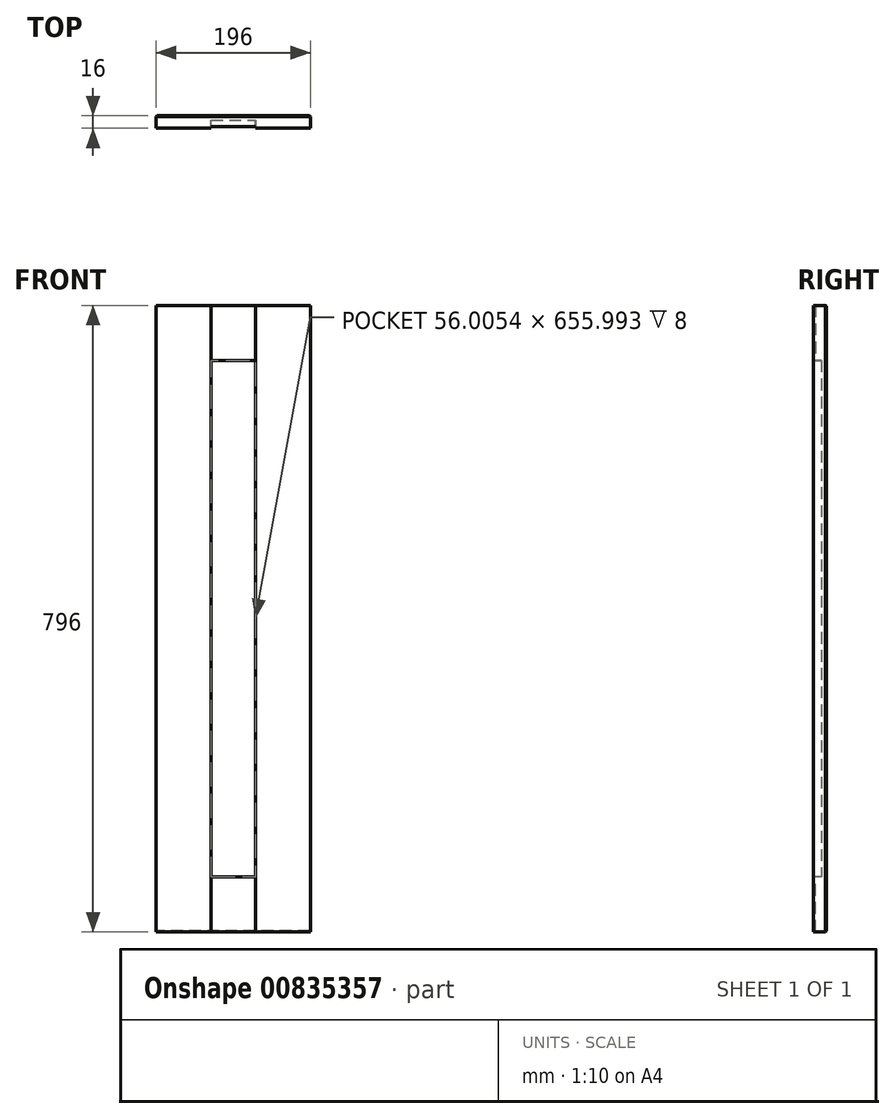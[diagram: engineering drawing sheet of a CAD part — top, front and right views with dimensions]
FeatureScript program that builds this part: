
annotation { "Feature Type Name" : "Feature", "Feature Type Description" : "" }
export const myFeature = defineFeature(function(context is Context, id is Id, definition is map)
    precondition{}
    {
        {
            var Q0;
            Q0=qCreatedBy(makeId("Front.planeOp"),FACE);
            var sketch = newSketch(context, id + "F0", { "sketchPlane" : qUnion([Q0])});
            skLineSegment(sketch, "E0.bottom", {"start": v(0, 0) * mm, "end": v(35.9, 0) * mm});
            skLineSegment(sketch, "E0.top", {"start": v(0, 30.12) * mm, "end": v(35.9, 30.12) * mm});
            skLineSegment(sketch, "E0.left", {"start": v(0, 0) * mm, "end": v(0, 30.12) * mm});
            skLineSegment(sketch, "E0.right", {"start": v(35.9, 0) * mm, "end": v(35.9, 30.12) * mm});
            skSolve(sketch);
        }
        {
            var Q0;
            Q0=makeQuery(id+"F0.imprint","IMPRINT",FACE,{"disambiguationData":[TD([[makeQuery(id+"F0.imprint","IMPRINT",EDGE,{"derivedFrom":sQuery(id+"F0.wireOp",EDGE,"E0.bottom")}),1.0]])]});
            extrude(context, id + "F1", {"entities" : qUnion([Q0]), "depth" : 16 * mm, "offsetDistance" : 25.4 * mm});
        }
        {
            var Q0;
            Q0=makeQuery(id+"F1.opExtrude","SWEPT_FACE",FACE,{"disambiguationData":[OSD([sQuery(id+"F0.wireOp",EDGE,"E0.left")])]});
            extrude(context, id + "F2", {"entities" : qUnion([Q0]), "operationType" : NewBodyOperationType.ADD, "oppositeDirection" : true, "depth" : 196 * mm, "offsetDistance" : 25 * mm});
        }
        {
            var Q0;
            {var subQ0=sQuery(id+"F0.wireOp",EDGE,"E0.bottom");Q0=makeQuery(id+"F2.boolean.opBoolean","MERGE",FACE,{"derivedFrom":[makeQuery(id+"F1.opExtrude","SWEPT_FACE",FACE,{"disambiguationData":[OSD([subQ0])]}),makeQuery(id+"F2.opExtrude","SWEPT_FACE",FACE,{"disambiguationData":[OSD([subQ0,sQuery(id+"F0.wireOp",EDGE,"E0.left")])]})]});}
            extrude(context, id + "F3", {"entities" : qUnion([Q0]), "operationType" : NewBodyOperationType.ADD, "oppositeDirection" : true, "depth" : 796 * mm, "offsetDistance" : 25 * mm});
        }
        {
            var Q0;
            {var subQ0=sQuery(id+"F0.wireOp",EDGE,"E0.left");var subQ1=sQuery(id+"F0.wireOp",EDGE,"E0.bottom");Q0=makeQuery(id+"F3.boolean.opBoolean","MERGE",FACE,{"derivedFrom":[makeQuery(id+"F2.boolean.opBoolean","MERGE",FACE,{"derivedFrom":[makeQuery(id+"F1.opExtrude","CAP_FACE",FACE,{"disambiguationData":[OSD([subQ1,sQuery(id+"F0.wireOp",EDGE,"E0.top"),subQ0,sQuery(id+"F0.wireOp",EDGE,"E0.right")])],"isStart":false}),makeQuery(id+"F2.opExtrude","SWEPT_FACE",FACE,{"disambiguationData":[OSD([subQ0]),TDD([makeQuery(id+"F1.opExtrude","CAP_EDGE",EDGE,{"disambiguationData":[OSD([subQ0])],"isStart":false})])]})]}),makeQuery(id+"F3.opExtrude","SWEPT_FACE",FACE,{"disambiguationData":[OSD([subQ1,subQ0]),TDD([makeQuery(id+"F2.boolean.opBoolean","MERGE",EDGE,{"derivedFrom":[makeQuery(id+"F1.opExtrude","CAP_EDGE",EDGE,{"disambiguationData":[OSD([subQ1])],"isStart":false}),makeQuery(id+"F2.opExtrude","SWEPT_EDGE",EDGE,{"disambiguationData":[OSD([subQ1,subQ0]),TDD([makeQuery(id+"F1.opExtrude","CAP_VERTEX",VERTEX,{"disambiguationData":[OSD([subQ1,subQ0])],"isStart":false})])]})]})])]})]});}
            var sketch = newSketch(context, id + "F4", { "sketchPlane" : qUnion([Q0])});
            skLineSegment(sketch, "E1.bottom", {"start": v(0, 796) * mm, "end": v(42.19, 796) * mm});
            skLineSegment(sketch, "E1.top", {"start": v(0, 751.57) * mm, "end": v(42.19, 751.57) * mm});
            skLineSegment(sketch, "E1.left", {"start": v(0, 796) * mm, "end": v(0, 751.57) * mm});
            skLineSegment(sketch, "E1.right", {"start": v(42.19, 796) * mm, "end": v(42.19, 751.57) * mm});
            skLineSegment(sketch, "E2.bottom", {"start": v(196, 796) * mm, "end": v(153.6, 796) * mm});
            skLineSegment(sketch, "E2.top", {"start": v(196, 746.75) * mm, "end": v(153.6, 746.75) * mm});
            skLineSegment(sketch, "E2.left", {"start": v(196, 796) * mm, "end": v(196, 746.75) * mm});
            skLineSegment(sketch, "E2.right", {"start": v(153.6, 796) * mm, "end": v(153.6, 746.75) * mm});
            skSolve(sketch);
        }
        {
            var Q0;
            Q0=makeQuery(id+"F4.imprint","IMPRINT",FACE,{"disambiguationData":[TD([[makeQuery(id+"F4.imprint","IMPRINT",EDGE,{"derivedFrom":sQuery(id+"F4.wireOp",EDGE,"E1.bottom")}),-1.0]])]});
            var Q1;
            Q1=makeQuery(id+"F4.imprint","IMPRINT",FACE,{"disambiguationData":[TD([[makeQuery(id+"F4.imprint","IMPRINT",EDGE,{"derivedFrom":sQuery(id+"F4.wireOp",EDGE,"E2.bottom")}),-1.0]])]});
            extrude(context, id + "F5", {"entities" : qUnion([Q0, Q1]), "operationType" : NewBodyOperationType.ADD, "depth" : 25 * mm, "offsetDistance" : 25 * mm});
        }
        {
            var Q0;
            {var subQ0=sQuery(id+"F0.wireOp",EDGE,"E0.left");var subQ1=sQuery(id+"F0.wireOp",EDGE,"E0.bottom");Q0=makeQuery(id+"F3.boolean.opBoolean","MERGE",FACE,{"derivedFrom":[makeQuery(id+"F2.boolean.opBoolean","MERGE",FACE,{"derivedFrom":[makeQuery(id+"F1.opExtrude","CAP_FACE",FACE,{"disambiguationData":[OSD([subQ1,sQuery(id+"F0.wireOp",EDGE,"E0.top"),subQ0,sQuery(id+"F0.wireOp",EDGE,"E0.right")])],"isStart":false}),makeQuery(id+"F2.opExtrude","SWEPT_FACE",FACE,{"disambiguationData":[OSD([subQ0]),TDD([makeQuery(id+"F1.opExtrude","CAP_EDGE",EDGE,{"disambiguationData":[OSD([subQ0])],"isStart":false})])]})]}),makeQuery(id+"F3.opExtrude","SWEPT_FACE",FACE,{"disambiguationData":[OSD([subQ1,subQ0]),TDD([makeQuery(id+"F2.boolean.opBoolean","MERGE",EDGE,{"derivedFrom":[makeQuery(id+"F1.opExtrude","CAP_EDGE",EDGE,{"disambiguationData":[OSD([subQ1])],"isStart":false}),makeQuery(id+"F2.opExtrude","SWEPT_EDGE",EDGE,{"disambiguationData":[OSD([subQ1,subQ0]),TDD([makeQuery(id+"F1.opExtrude","CAP_VERTEX",VERTEX,{"disambiguationData":[OSD([subQ1,subQ0])],"isStart":false})])]})]})])]})]});}
            var sketch = newSketch(context, id + "F6", { "sketchPlane" : qUnion([Q0])});
            skLineSegment(sketch, "E3.bottom", {"start": v(196, 0) * mm, "end": v(163.38, 0) * mm});
            skLineSegment(sketch, "E3.top", {"start": v(196, 46.55) * mm, "end": v(163.38, 46.55) * mm});
            skLineSegment(sketch, "E3.left", {"start": v(196, 0) * mm, "end": v(196, 46.55) * mm});
            skLineSegment(sketch, "E3.right", {"start": v(163.38, 0) * mm, "end": v(163.38, 46.55) * mm});
            skLineSegment(sketch, "E4.bottom", {"start": v(0, 0) * mm, "end": v(50.28, 0) * mm});
            skLineSegment(sketch, "E4.top", {"start": v(0, 44.4) * mm, "end": v(50.28, 44.4) * mm});
            skLineSegment(sketch, "E4.left", {"start": v(0, 0) * mm, "end": v(0, 44.4) * mm});
            skLineSegment(sketch, "E4.right", {"start": v(50.28, 0) * mm, "end": v(50.28, 44.4) * mm});
            skSolve(sketch);
        }
        {
            var Q0;
            Q0=makeQuery(id+"F6.imprint","IMPRINT",FACE,{"disambiguationData":[TD([[makeQuery(id+"F6.imprint","IMPRINT",EDGE,{"derivedFrom":sQuery(id+"F6.wireOp",EDGE,"E3.bottom")}),1.0]])]});
            var Q1;
            Q1=makeQuery(id+"F6.imprint","IMPRINT",FACE,{"disambiguationData":[TD([[makeQuery(id+"F6.imprint","IMPRINT",EDGE,{"derivedFrom":sQuery(id+"F6.wireOp",EDGE,"E4.bottom")}),1.0]])]});
            extrude(context, id + "F7", {"entities" : qUnion([Q0, Q1]), "operationType" : NewBodyOperationType.ADD, "depth" : 25 * mm, "offsetDistance" : 25 * mm});
        }
        {
            var Q0;
            Q0=makeQuery(id+"F7.opExtrude","SWEPT_FACE",FACE,{"disambiguationData":[OSD([sQuery(id+"F6.wireOp",EDGE,"E4.right")])]});
            extrude(context, id + "F8", {"entities" : qUnion([Q0]), "operationType" : NewBodyOperationType.ADD, "depth" : 19.72 * mm, "offsetDistance" : 25 * mm});
        }
        {
            var Q0;
            {var subQ0=sQuery(id+"F6.wireOp",EDGE,"E4.top");Q0=makeQuery(id+"F8.boolean.opBoolean","MERGE",FACE,{"derivedFrom":[makeQuery(id+"F7.opExtrude","SWEPT_FACE",FACE,{"disambiguationData":[OSD([subQ0])]}),makeQuery(id+"F8.opExtrude","SWEPT_FACE",FACE,{"disambiguationData":[OSD([subQ0,sQuery(id+"F6.wireOp",EDGE,"E4.right")])]})]});}
            extrude(context, id + "F9", {"entities" : qUnion([Q0]), "operationType" : NewBodyOperationType.ADD, "depth" : 25.6 * mm, "offsetDistance" : 25 * mm});
        }
        {
            var Q0;
            Q0=makeQuery(id+"F7.opExtrude","SWEPT_FACE",FACE,{"disambiguationData":[OSD([sQuery(id+"F6.wireOp",EDGE,"E3.right")])]});
            extrude(context, id + "F10", {"entities" : qUnion([Q0]), "operationType" : NewBodyOperationType.ADD, "depth" : 37.38 * mm, "offsetDistance" : 25 * mm});
        }
        {
            var Q0;
            {var subQ0=sQuery(id+"F6.wireOp",EDGE,"E3.top");Q0=makeQuery(id+"F10.boolean.opBoolean","MERGE",FACE,{"derivedFrom":[makeQuery(id+"F7.opExtrude","SWEPT_FACE",FACE,{"disambiguationData":[OSD([subQ0])]}),makeQuery(id+"F10.opExtrude","SWEPT_FACE",FACE,{"disambiguationData":[OSD([subQ0,sQuery(id+"F6.wireOp",EDGE,"E3.right")])]})]});}
            extrude(context, id + "F11", {"entities" : qUnion([Q0]), "operationType" : NewBodyOperationType.ADD, "depth" : 23.45 * mm, "offsetDistance" : 25 * mm});
        }
        {
            var Q0;
            Q0=makeQuery(id+"F5.opExtrude","SWEPT_FACE",FACE,{"disambiguationData":[OSD([sQuery(id+"F4.wireOp",EDGE,"E1.right")])]});
            extrude(context, id + "F12", {"entities" : qUnion([Q0]), "operationType" : NewBodyOperationType.ADD, "depth" : 27.8 * mm, "offsetDistance" : 25 * mm});
        }
        {
            var Q0;
            {var subQ0=sQuery(id+"F4.wireOp",EDGE,"E1.top");Q0=makeQuery(id+"F12.boolean.opBoolean","MERGE",FACE,{"derivedFrom":[makeQuery(id+"F5.opExtrude","SWEPT_FACE",FACE,{"disambiguationData":[OSD([subQ0])]}),makeQuery(id+"F12.opExtrude","SWEPT_FACE",FACE,{"disambiguationData":[OSD([subQ0,sQuery(id+"F4.wireOp",EDGE,"E1.right")])]})]});}
            extrude(context, id + "F13", {"entities" : qUnion([Q0]), "operationType" : NewBodyOperationType.ADD, "depth" : 25.57 * mm, "offsetDistance" : 25 * mm});
        }
        {
            var Q0;
            Q0=makeQuery(id+"F5.opExtrude","SWEPT_FACE",FACE,{"disambiguationData":[OSD([sQuery(id+"F4.wireOp",EDGE,"E2.top")])]});
            extrude(context, id + "F14", {"entities" : qUnion([Q0]), "operationType" : NewBodyOperationType.ADD, "depth" : 20.75 * mm, "offsetDistance" : 25 * mm});
        }
        {
            var Q0;
            {var subQ0=sQuery(id+"F4.wireOp",EDGE,"E2.right");Q0=makeQuery(id+"F14.boolean.opBoolean","MERGE",FACE,{"derivedFrom":[makeQuery(id+"F5.opExtrude","SWEPT_FACE",FACE,{"disambiguationData":[OSD([subQ0])]}),makeQuery(id+"F14.opExtrude","SWEPT_FACE",FACE,{"disambiguationData":[OSD([sQuery(id+"F4.wireOp",EDGE,"E2.top"),subQ0])]})]});}
            extrude(context, id + "F15", {"entities" : qUnion([Q0]), "operationType" : NewBodyOperationType.ADD, "depth" : 27.6 * mm, "offsetDistance" : 25 * mm});
        }
        {
            var Q0;
            {var subQ0=sQuery(id+"F0.wireOp",EDGE,"E0.left");var subQ1=sQuery(id+"F0.wireOp",EDGE,"E0.bottom");Q0=makeQuery(id+"F3.boolean.opBoolean","MERGE",FACE,{"derivedFrom":[makeQuery(id+"F2.boolean.opBoolean","MERGE",FACE,{"derivedFrom":[makeQuery(id+"F1.opExtrude","CAP_FACE",FACE,{"disambiguationData":[OSD([subQ1,sQuery(id+"F0.wireOp",EDGE,"E0.top"),subQ0,sQuery(id+"F0.wireOp",EDGE,"E0.right")])],"isStart":false}),makeQuery(id+"F2.opExtrude","SWEPT_FACE",FACE,{"disambiguationData":[OSD([subQ0]),TDD([makeQuery(id+"F1.opExtrude","CAP_EDGE",EDGE,{"disambiguationData":[OSD([subQ0])],"isStart":false})])]})]}),makeQuery(id+"F3.opExtrude","SWEPT_FACE",FACE,{"disambiguationData":[OSD([subQ1,subQ0]),TDD([makeQuery(id+"F2.boolean.opBoolean","MERGE",EDGE,{"derivedFrom":[makeQuery(id+"F1.opExtrude","CAP_EDGE",EDGE,{"disambiguationData":[OSD([subQ1])],"isStart":false}),makeQuery(id+"F2.opExtrude","SWEPT_EDGE",EDGE,{"disambiguationData":[OSD([subQ1,subQ0]),TDD([makeQuery(id+"F1.opExtrude","CAP_VERTEX",VERTEX,{"disambiguationData":[OSD([subQ1,subQ0])],"isStart":false})])]})]})])]})]});}
            var sketch = newSketch(context, id + "F16", { "sketchPlane" : qUnion([Q0])});
            skLineSegment(sketch, "E5.bottom", {"start": v(70, 726) * mm, "end": v(126, 726) * mm});
            skLineSegment(sketch, "E5.top", {"start": v(70, 70) * mm, "end": v(126, 70) * mm});
            skLineSegment(sketch, "E5.left", {"start": v(70, 726) * mm, "end": v(70, 70) * mm});
            skLineSegment(sketch, "E5.right", {"start": v(126, 726) * mm, "end": v(126, 70) * mm});
            skSolve(sketch);
        }
        {
            var Q0;
            Q0=makeQuery(id+"F16.imprint","IMPRINT",FACE,{"disambiguationData":[TD([[makeQuery(id+"F16.imprint","IMPRINT",EDGE,{"derivedFrom":sQuery(id+"F16.wireOp",EDGE,"E5.top")}),1.0]])]});
            extrude(context, id + "F17", {"entities" : qUnion([Q0]), "operationType" : NewBodyOperationType.REMOVE, "oppositeDirection" : true, "depth" : 10 * mm, "offsetDistance" : 25 * mm});
        }
        {
            var Q0;
            {var subQ2=sQuery(id+"F0.wireOp",EDGE,"E0.left");var subQ3=sQuery(id+"F0.wireOp",EDGE,"E0.bottom");var subQ4=makeQuery(id+"F1.opExtrude","CAP_FACE",FACE,{"disambiguationData":[OSD([subQ3,sQuery(id+"F0.wireOp",EDGE,"E0.top"),subQ2,sQuery(id+"F0.wireOp",EDGE,"E0.right")])],"isStart":false});var subQ7=makeQuery(id+"F3.opExtrude","SWEPT_FACE",FACE,{"disambiguationData":[OSD([subQ3,subQ2]),TDD([makeQuery(id+"F2.boolean.opBoolean","MERGE",EDGE,{"derivedFrom":[makeQuery(id+"F1.opExtrude","CAP_EDGE",EDGE,{"disambiguationData":[OSD([subQ3])],"isStart":false}),makeQuery(id+"F2.opExtrude","SWEPT_EDGE",EDGE,{"disambiguationData":[OSD([subQ3,subQ2]),TDD([makeQuery(id+"F1.opExtrude","CAP_VERTEX",VERTEX,{"disambiguationData":[OSD([subQ3,subQ2])],"isStart":false})])]})]})])]});var subQ8=makeQuery(id+"F2.opExtrude","SWEPT_FACE",FACE,{"disambiguationData":[OSD([subQ2]),TDD([makeQuery(id+"F1.opExtrude","CAP_EDGE",EDGE,{"disambiguationData":[OSD([subQ2])],"isStart":false})])]});Q0=makeQuery(id+"F17.boolean.opBoolean","SPLIT",FACE,{"disambiguationData":[TD([makeQuery(id+"F1.opExtrude","SWEPT_FACE",FACE,{"disambiguationData":[OSD([subQ3])]})])],"derivedFrom":makeQuery(id+"F3.boolean.opBoolean","MERGE",FACE,{"derivedFrom":[makeQuery(id+"F2.boolean.opBoolean","MERGE",FACE,{"derivedFrom":[subQ4,subQ8]}),subQ7]})});}
            var Q1;
            {var subQ2=sQuery(id+"F4.wireOp",EDGE,"E1.bottom");var subQ3=sQuery(id+"F0.wireOp",EDGE,"E0.left");var subQ4=sQuery(id+"F0.wireOp",EDGE,"E0.bottom");var subQ6=makeQuery(id+"F1.opExtrude","CAP_FACE",FACE,{"disambiguationData":[OSD([subQ4,sQuery(id+"F0.wireOp",EDGE,"E0.top"),subQ3,sQuery(id+"F0.wireOp",EDGE,"E0.right")])],"isStart":false});var subQ7=makeQuery(id+"F2.opExtrude","SWEPT_FACE",FACE,{"disambiguationData":[OSD([subQ3]),TDD([makeQuery(id+"F1.opExtrude","CAP_EDGE",EDGE,{"disambiguationData":[OSD([subQ3])],"isStart":false})])]});var subQ8=makeQuery(id+"F3.opExtrude","SWEPT_FACE",FACE,{"disambiguationData":[OSD([subQ4,subQ3]),TDD([makeQuery(id+"F2.boolean.opBoolean","MERGE",EDGE,{"derivedFrom":[makeQuery(id+"F1.opExtrude","CAP_EDGE",EDGE,{"disambiguationData":[OSD([subQ4])],"isStart":false}),makeQuery(id+"F2.opExtrude","SWEPT_EDGE",EDGE,{"disambiguationData":[OSD([subQ4,subQ3]),TDD([makeQuery(id+"F1.opExtrude","CAP_VERTEX",VERTEX,{"disambiguationData":[OSD([subQ4,subQ3])],"isStart":false})])]})]})])]});Q1=makeQuery(id+"F17.boolean.opBoolean","SPLIT",FACE,{"disambiguationData":[TD([makeQuery(id+"F5.opExtrude","SWEPT_FACE",FACE,{"disambiguationData":[OSD([subQ2])]})])],"derivedFrom":makeQuery(id+"F3.boolean.opBoolean","MERGE",FACE,{"derivedFrom":[makeQuery(id+"F2.boolean.opBoolean","MERGE",FACE,{"derivedFrom":[subQ6,subQ7]}),subQ8]})});}
            extrude(context, id + "F18", {"entities" : qUnion([Q0, Q1]), "operationType" : NewBodyOperationType.REMOVE, "oppositeDirection" : true, "depth" : 2 * mm, "offsetDistance" : 25 * mm});
        }
        {
            var Q0;
            {var subQ0=sQuery(id+"F4.wireOp",EDGE,"E1.right");var subQ1=sQuery(id+"F4.wireOp",EDGE,"E1.top");Q0=makeQuery(id+"F13.boolean.opBoolean","MERGE",FACE,{"derivedFrom":[makeQuery(id+"F12.boolean.opBoolean","MERGE",FACE,{"derivedFrom":[makeQuery(id+"F5.opExtrude","CAP_FACE",FACE,{"disambiguationData":[OSD([sQuery(id+"F4.wireOp",EDGE,"E1.bottom"),subQ1,sQuery(id+"F4.wireOp",EDGE,"E1.left"),subQ0])],"isStart":false}),makeQuery(id+"F12.opExtrude","SWEPT_FACE",FACE,{"disambiguationData":[OSD([subQ0]),TDD([makeQuery(id+"F5.opExtrude","CAP_EDGE",EDGE,{"disambiguationData":[OSD([subQ0])],"isStart":false})])]})]}),makeQuery(id+"F13.opExtrude","SWEPT_FACE",FACE,{"disambiguationData":[OSD([subQ1,subQ0]),TDD([makeQuery(id+"F12.boolean.opBoolean","MERGE",EDGE,{"derivedFrom":[makeQuery(id+"F5.opExtrude","CAP_EDGE",EDGE,{"disambiguationData":[OSD([subQ1])],"isStart":false}),makeQuery(id+"F12.opExtrude","SWEPT_EDGE",EDGE,{"disambiguationData":[OSD([subQ1,subQ0]),TDD([makeQuery(id+"F5.opExtrude","CAP_VERTEX",VERTEX,{"disambiguationData":[OSD([subQ1,subQ0])],"isStart":false})])]})]})])]})]});}
            var Q1;
            {var subQ0=sQuery(id+"F4.wireOp",EDGE,"E2.right");var subQ1=sQuery(id+"F4.wireOp",EDGE,"E2.top");Q1=makeQuery(id+"F15.boolean.opBoolean","MERGE",FACE,{"derivedFrom":[makeQuery(id+"F14.boolean.opBoolean","MERGE",FACE,{"derivedFrom":[makeQuery(id+"F5.opExtrude","CAP_FACE",FACE,{"disambiguationData":[OSD([sQuery(id+"F4.wireOp",EDGE,"E2.bottom"),subQ1,sQuery(id+"F4.wireOp",EDGE,"E2.left"),subQ0])],"isStart":false}),makeQuery(id+"F14.opExtrude","SWEPT_FACE",FACE,{"disambiguationData":[OSD([subQ1]),TDD([makeQuery(id+"F5.opExtrude","CAP_EDGE",EDGE,{"disambiguationData":[OSD([subQ1])],"isStart":false})])]})]}),makeQuery(id+"F15.opExtrude","SWEPT_FACE",FACE,{"disambiguationData":[OSD([subQ1,subQ0]),TDD([makeQuery(id+"F14.boolean.opBoolean","MERGE",EDGE,{"derivedFrom":[makeQuery(id+"F5.opExtrude","CAP_EDGE",EDGE,{"disambiguationData":[OSD([subQ0])],"isStart":false}),makeQuery(id+"F14.opExtrude","SWEPT_EDGE",EDGE,{"disambiguationData":[OSD([subQ1,subQ0]),TDD([makeQuery(id+"F5.opExtrude","CAP_VERTEX",VERTEX,{"disambiguationData":[OSD([subQ1,subQ0])],"isStart":false})])]})]})])]})]});}
            var Q2;
            {var subQ0=sQuery(id+"F6.wireOp",EDGE,"E4.right");var subQ1=sQuery(id+"F6.wireOp",EDGE,"E4.top");Q2=makeQuery(id+"F9.boolean.opBoolean","MERGE",FACE,{"derivedFrom":[makeQuery(id+"F8.boolean.opBoolean","MERGE",FACE,{"derivedFrom":[makeQuery(id+"F7.opExtrude","CAP_FACE",FACE,{"disambiguationData":[OSD([sQuery(id+"F6.wireOp",EDGE,"E4.bottom"),subQ1,sQuery(id+"F6.wireOp",EDGE,"E4.left"),subQ0])],"isStart":false}),makeQuery(id+"F8.opExtrude","SWEPT_FACE",FACE,{"disambiguationData":[OSD([subQ0]),TDD([makeQuery(id+"F7.opExtrude","CAP_EDGE",EDGE,{"disambiguationData":[OSD([subQ0])],"isStart":false})])]})]}),makeQuery(id+"F9.opExtrude","SWEPT_FACE",FACE,{"disambiguationData":[OSD([subQ1,subQ0]),TDD([makeQuery(id+"F8.boolean.opBoolean","MERGE",EDGE,{"derivedFrom":[makeQuery(id+"F7.opExtrude","CAP_EDGE",EDGE,{"disambiguationData":[OSD([subQ1])],"isStart":false}),makeQuery(id+"F8.opExtrude","SWEPT_EDGE",EDGE,{"disambiguationData":[OSD([subQ1,subQ0]),TDD([makeQuery(id+"F7.opExtrude","CAP_VERTEX",VERTEX,{"disambiguationData":[OSD([subQ1,subQ0])],"isStart":false})])]})]})])]})]});}
            var Q3;
            {var subQ0=sQuery(id+"F6.wireOp",EDGE,"E3.right");var subQ1=sQuery(id+"F6.wireOp",EDGE,"E3.top");Q3=makeQuery(id+"F11.boolean.opBoolean","MERGE",FACE,{"derivedFrom":[makeQuery(id+"F10.boolean.opBoolean","MERGE",FACE,{"derivedFrom":[makeQuery(id+"F7.opExtrude","CAP_FACE",FACE,{"disambiguationData":[OSD([sQuery(id+"F6.wireOp",EDGE,"E3.bottom"),subQ1,sQuery(id+"F6.wireOp",EDGE,"E3.left"),subQ0])],"isStart":false}),makeQuery(id+"F10.opExtrude","SWEPT_FACE",FACE,{"disambiguationData":[OSD([subQ0]),TDD([makeQuery(id+"F7.opExtrude","CAP_EDGE",EDGE,{"disambiguationData":[OSD([subQ0])],"isStart":false})])]})]}),makeQuery(id+"F11.opExtrude","SWEPT_FACE",FACE,{"disambiguationData":[OSD([subQ1,subQ0]),TDD([makeQuery(id+"F10.boolean.opBoolean","MERGE",EDGE,{"derivedFrom":[makeQuery(id+"F7.opExtrude","CAP_EDGE",EDGE,{"disambiguationData":[OSD([subQ1])],"isStart":false}),makeQuery(id+"F10.opExtrude","SWEPT_EDGE",EDGE,{"disambiguationData":[OSD([subQ1,subQ0]),TDD([makeQuery(id+"F7.opExtrude","CAP_VERTEX",VERTEX,{"disambiguationData":[OSD([subQ1,subQ0])],"isStart":false})])]})]})])]})]});}
            extrude(context, id + "F19", {"entities" : qUnion([Q0, Q1, Q2, Q3]), "operationType" : NewBodyOperationType.REMOVE, "oppositeDirection" : true, "depth" : 25 * mm, "offsetDistance" : 25 * mm});
        }
        {
            var Q0;
            {var subQ0=sQuery(id+"F0.wireOp",EDGE,"E0.left");var subQ1=sQuery(id+"F0.wireOp",EDGE,"E0.bottom");Q0=makeQuery(id+"F19.boolean.opBoolean","MERGE",EDGE,{"derivedFrom":[makeQuery(id+"F3.boolean.opBoolean","MERGE",EDGE,{"derivedFrom":[makeQuery(id+"F2.opExtrude","CAP_EDGE",EDGE,{"disambiguationData":[OSD([subQ0]),TDD([makeQuery(id+"F1.opExtrude","CAP_EDGE",EDGE,{"disambiguationData":[OSD([subQ0])],"isStart":false})])],"isStart":false}),makeQuery(id+"F3.opExtrude","SWEPT_EDGE",EDGE,{"disambiguationData":[OSD([subQ1,subQ0]),TDD([makeQuery(id+"F2.opExtrude","CAP_VERTEX",VERTEX,{"disambiguationData":[OSD([subQ1,subQ0]),TDD([makeQuery(id+"F1.opExtrude","CAP_VERTEX",VERTEX,{"disambiguationData":[OSD([subQ1,subQ0])],"isStart":false})])],"isStart":false})])]})]}),makeQuery(id+"F19.opExtrude","CAP_EDGE",EDGE,{"disambiguationData":[OSD([subQ1,subQ0,sQuery(id+"F6.wireOp",EDGE,"E3.top"),sQuery(id+"F6.wireOp",EDGE,"E3.left")])],"isStart":false}),makeQuery(id+"F19.opExtrude","CAP_EDGE",EDGE,{"disambiguationData":[OSD([subQ1,subQ0,sQuery(id+"F4.wireOp",EDGE,"E2.top"),sQuery(id+"F4.wireOp",EDGE,"E2.left")])],"isStart":false})]});}
            var Q1;
            Q1=makeQuery(id+"F19.boolean.opBoolean","COPY",EDGE,{"derivedFrom":makeQuery(id+"F19.opExtrude","CAP_EDGE",EDGE,{"disambiguationData":[OSD([sQuery(id+"F0.wireOp",EDGE,"E0.bottom"),sQuery(id+"F0.wireOp",EDGE,"E0.left"),sQuery(id+"F6.wireOp",EDGE,"E3.bottom"),sQuery(id+"F6.wireOp",EDGE,"E3.right")])],"isStart":false})});
            var Q2;
            Q2=makeQuery(id+"F19.boolean.opBoolean","COPY",EDGE,{"derivedFrom":makeQuery(id+"F19.opExtrude","CAP_EDGE",EDGE,{"disambiguationData":[OSD([sQuery(id+"F0.wireOp",EDGE,"E0.bottom"),sQuery(id+"F0.wireOp",EDGE,"E0.left"),sQuery(id+"F6.wireOp",EDGE,"E4.bottom"),sQuery(id+"F6.wireOp",EDGE,"E4.right")])],"isStart":false})});
            var Q3;
            {var subQ0=sQuery(id+"F0.wireOp",EDGE,"E0.left");var subQ1=sQuery(id+"F0.wireOp",EDGE,"E0.bottom");Q3=makeQuery(id+"F19.boolean.opBoolean","MERGE",EDGE,{"derivedFrom":[makeQuery(id+"F3.boolean.opBoolean","MERGE",EDGE,{"derivedFrom":[makeQuery(id+"F1.opExtrude","CAP_EDGE",EDGE,{"disambiguationData":[OSD([subQ0])],"isStart":false}),makeQuery(id+"F3.opExtrude","SWEPT_EDGE",EDGE,{"disambiguationData":[OSD([subQ1,subQ0]),TDD([makeQuery(id+"F1.opExtrude","CAP_VERTEX",VERTEX,{"disambiguationData":[OSD([subQ1,subQ0])],"isStart":false})])]})]}),makeQuery(id+"F19.opExtrude","CAP_EDGE",EDGE,{"disambiguationData":[OSD([subQ1,subQ0,sQuery(id+"F6.wireOp",EDGE,"E4.top"),sQuery(id+"F6.wireOp",EDGE,"E4.left")])],"isStart":false}),makeQuery(id+"F19.opExtrude","CAP_EDGE",EDGE,{"disambiguationData":[OSD([subQ1,subQ0,sQuery(id+"F4.wireOp",EDGE,"E1.top"),sQuery(id+"F4.wireOp",EDGE,"E1.left")])],"isStart":false})]});}
            var Q4;
            Q4=makeQuery(id+"F19.boolean.opBoolean","COPY",EDGE,{"derivedFrom":makeQuery(id+"F19.opExtrude","CAP_EDGE",EDGE,{"disambiguationData":[OSD([sQuery(id+"F0.wireOp",EDGE,"E0.bottom"),sQuery(id+"F0.wireOp",EDGE,"E0.left"),sQuery(id+"F4.wireOp",EDGE,"E1.bottom"),sQuery(id+"F4.wireOp",EDGE,"E1.right")])],"isStart":false})});
            var Q5;
            Q5=makeQuery(id+"F19.boolean.opBoolean","COPY",EDGE,{"derivedFrom":makeQuery(id+"F19.opExtrude","CAP_EDGE",EDGE,{"disambiguationData":[OSD([sQuery(id+"F0.wireOp",EDGE,"E0.bottom"),sQuery(id+"F0.wireOp",EDGE,"E0.left"),sQuery(id+"F4.wireOp",EDGE,"E2.bottom"),sQuery(id+"F4.wireOp",EDGE,"E2.right")])],"isStart":false})});
            var Q6;
            {var subQ0=sQuery(id+"F0.wireOp",EDGE,"E0.left");var subQ1=sQuery(id+"F0.wireOp",EDGE,"E0.bottom");Q6=makeQuery(id+"F3.boolean.opBoolean","MERGE",FACE,{"derivedFrom":[makeQuery(id+"F2.boolean.opBoolean","MERGE",FACE,{"derivedFrom":[makeQuery(id+"F1.opExtrude","CAP_FACE",FACE,{"disambiguationData":[OSD([subQ1,sQuery(id+"F0.wireOp",EDGE,"E0.top"),subQ0,sQuery(id+"F0.wireOp",EDGE,"E0.right")])],"isStart":true}),makeQuery(id+"F2.opExtrude","SWEPT_FACE",FACE,{"disambiguationData":[OSD([subQ0]),TDD([makeQuery(id+"F1.opExtrude","CAP_EDGE",EDGE,{"disambiguationData":[OSD([subQ0])],"isStart":true})])]})]}),makeQuery(id+"F3.opExtrude","SWEPT_FACE",FACE,{"disambiguationData":[OSD([subQ1,subQ0]),TDD([makeQuery(id+"F2.boolean.opBoolean","MERGE",EDGE,{"derivedFrom":[makeQuery(id+"F1.opExtrude","CAP_EDGE",EDGE,{"disambiguationData":[OSD([subQ1])],"isStart":true}),makeQuery(id+"F2.opExtrude","SWEPT_EDGE",EDGE,{"disambiguationData":[OSD([subQ1,subQ0]),TDD([makeQuery(id+"F1.opExtrude","CAP_VERTEX",VERTEX,{"disambiguationData":[OSD([subQ1,subQ0])],"isStart":true})])]})]})])]})]});}
            chamfer(context, id + "F20", {"entities" : qUnion([Q0, Q1, Q2, Q3, Q4, Q5, Q6]), "width" : 1 * mm, "tangentPropagation" : true});
        }
    });
